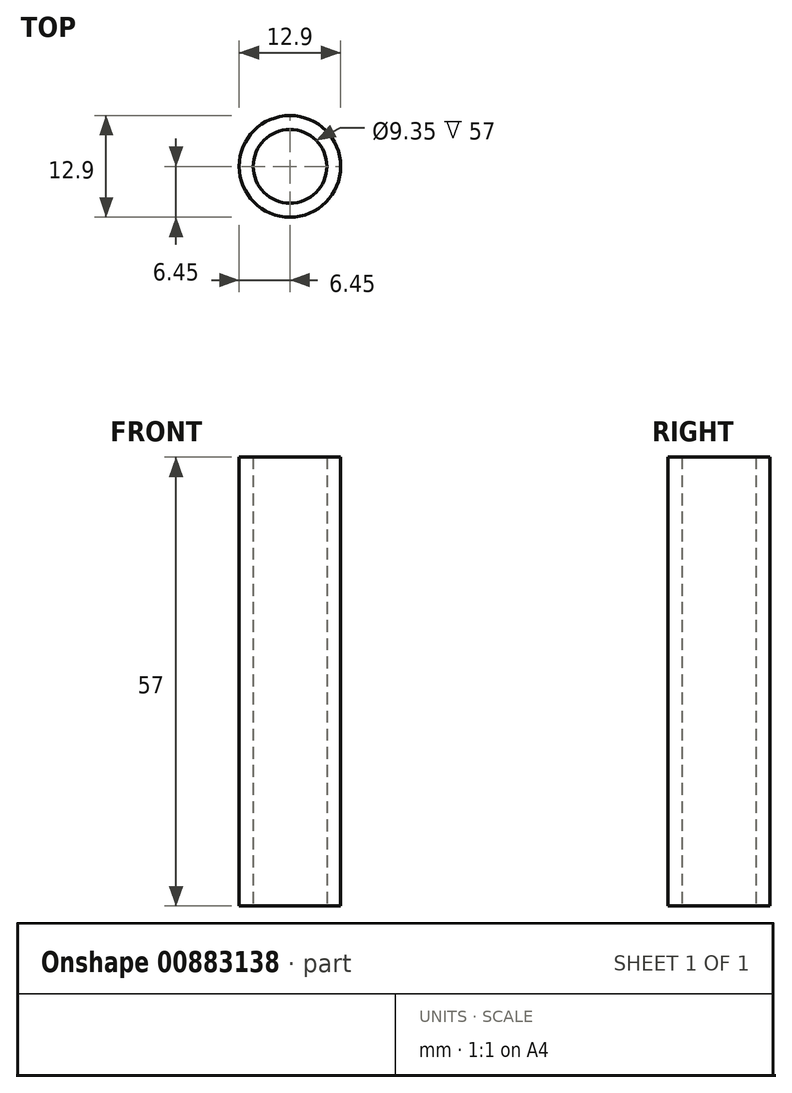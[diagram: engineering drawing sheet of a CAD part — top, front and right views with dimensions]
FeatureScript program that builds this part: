
annotation { "Feature Type Name" : "Feature", "Feature Type Description" : "" }
export const myFeature = defineFeature(function(context is Context, id is Id, definition is map)
    precondition{}
    {
        {
            var Q0;
            Q0=qCreatedBy(makeId("Top.planeOp"),FACE);
            var sketch = newSketch(context, id + "F0", { "sketchPlane" : qUnion([Q0])});
            skCircle(sketch, "E0", {"center": v(0, 0) * mm, "radius": 6.45 * mm});
            skCircle(sketch, "E1.0", {"center": v(0, 0) * mm, "radius": 4.68 * mm});
            skSolve(sketch);
        }
        {
            var Q0;
            Q0 = qSketchRegion(id + "F0", true);
            extrude(context, id + "F1", {"entities" : qUnion([Q0]), "depth" : 57 * mm, "offsetDistance" : 25 * mm});
        }
    });
